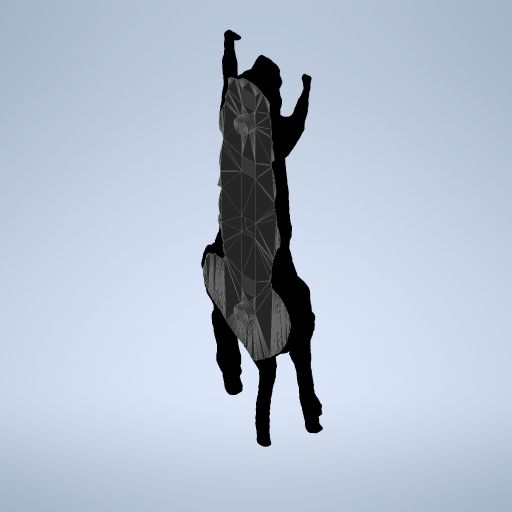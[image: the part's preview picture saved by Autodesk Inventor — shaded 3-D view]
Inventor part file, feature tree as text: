
AUTODESK INVENTOR PART (.ipt)
format: ipt  version: 2023 (Build 270158000, 158)  size: 2,344,960 bytes
history: native  units: in
note: dims shown in document units (in); Inventor stores cm internally (conversion verified against a paired STEP export)
features: other x2, extrude x1, sketch x1
ambient origin geometry x8: Origin, YZ Plane, XZ Plane, XY Plane, X Axis, Y Axis, Z Axis, Center Point
bodies: Solid1 (feature_tree)
feature tree (4):
  other  "prone_mouse_bottom_TLD"
  extrude  "Extrusion1"  Depth=0.0472in
  sketch  "Sketch1"  dims[d0=0.0472in d1=0.0in d2=0.0197in d3=0.0344in]
  other  "MeshFeature1"
